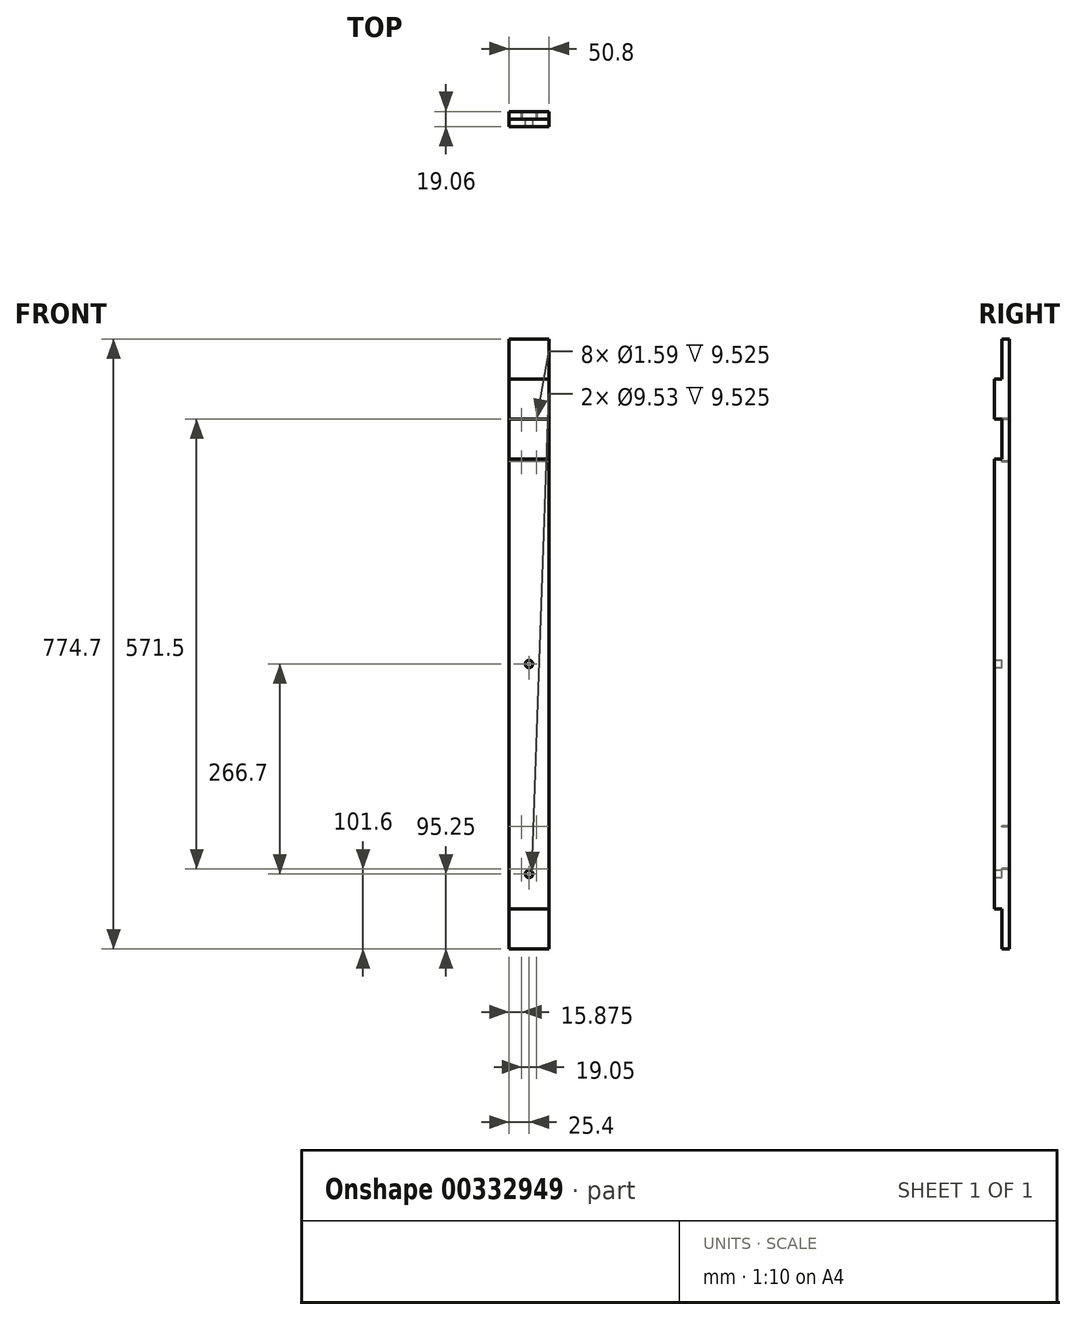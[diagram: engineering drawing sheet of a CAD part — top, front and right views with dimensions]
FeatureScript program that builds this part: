
annotation { "Feature Type Name" : "Feature", "Feature Type Description" : "" }
export const myFeature = defineFeature(function(context is Context, id is Id, definition is map)
    precondition{}
    {
        {
            var Q0;
            Q0=qCreatedBy(makeId("Top.planeOp"),FACE);
            var sketch = newSketch(context, id + "F0", { "sketchPlane" : qUnion([Q0])});
            skLineSegment(sketch, "E0.bottom", {"start": v(25.4, 9.53) * mm, "end": v(-25.4, 9.53) * mm});
            skLineSegment(sketch, "E0.top", {"start": v(25.4, -9.53) * mm, "end": v(-25.4, -9.53) * mm});
            skLineSegment(sketch, "E0.left", {"start": v(25.4, 9.53) * mm, "end": v(25.4, -9.52) * mm});
            skLineSegment(sketch, "E0.right", {"start": v(-25.4, 9.53) * mm, "end": v(-25.4, -9.53) * mm});
            skPoint(sketch, "E0.middle", {"position": v(0, 0) * mm});
            skSolve(sketch);
        }
        {
            var Q0;
            Q0=makeQuery(id+"F0.imprint","IMPRINT",FACE,{"disambiguationData":[TD([[makeQuery(id+"F0.imprint","IMPRINT",EDGE,{"derivedFrom":sQuery(id+"F0.wireOp",EDGE,"E0.bottom")}),1.0]])]});
            var Q1;
            Q1=qSketchRegion(id+"F2",true);
            extrude(context, id + "F1", {"entities" : qUnion([Q0, Q1]), "depth" : 774.7 * mm});
        }
        {
            var Q0;
            Q0=qCreatedBy(makeId("Front.planeOp"),FACE);
            var sketch = newSketch(context, id + "F2", { "sketchPlane" : qUnion([Q0])});
            skLineSegment(sketch, "E1.bottom", {"start": v(-38.77, 0) * mm, "end": v(83.66, 0) * mm});
            skLineSegment(sketch, "E1.top", {"start": v(-38.77, 50.8) * mm, "end": v(83.66, 50.8) * mm});
            skLineSegment(sketch, "E1.left", {"start": v(-38.77, 0) * mm, "end": v(-38.77, 50.8) * mm});
            skLineSegment(sketch, "E1.right", {"start": v(83.66, 0) * mm, "end": v(83.66, 50.8) * mm});
            skLineSegment(sketch, "E2.bottom", {"start": v(-210.36, 723.9) * mm, "end": v(132.8, 723.9) * mm});
            skLineSegment(sketch, "E2.top", {"start": v(-210.36, 774.7) * mm, "end": v(132.8, 774.7) * mm});
            skLineSegment(sketch, "E2.left", {"start": v(-210.36, 723.9) * mm, "end": v(-210.36, 774.7) * mm});
            skLineSegment(sketch, "E2.right", {"start": v(132.8, 723.9) * mm, "end": v(132.8, 774.7) * mm});
            skLineSegment(sketch, "E3.bottom", {"start": v(-160.47, 673.1) * mm, "end": v(92.9, 673.1) * mm});
            skLineSegment(sketch, "E3.top", {"start": v(-160.47, 622.3) * mm, "end": v(92.9, 622.3) * mm});
            skLineSegment(sketch, "E3.left", {"start": v(-160.47, 673.1) * mm, "end": v(-160.47, 622.3) * mm});
            skLineSegment(sketch, "E3.right", {"start": v(92.9, 673.1) * mm, "end": v(92.9, 622.3) * mm});
            skSolve(sketch);
        }
        {
            var Q0;
            Q0=qSketchRegion(id+"F2",true);
            extrude(context, id + "F3", {"entities" : qUnion([Q0]), "operationType" : NewBodyOperationType.REMOVE, "depth" : 25.4 * mm});
        }
        {
            var Q0;
            Q0=qCreatedBy(makeId("Front.planeOp"),FACE);
            var sketch = newSketch(context, id + "F4", { "sketchPlane" : qUnion([Q0])});
            skCircle(sketch, "E4", {"center": v(9.53, 101.6) * mm, "radius": 0.8 * mm});
            skCircle(sketch, "E5", {"center": v(9.52, 155.58) * mm, "radius": 0.8 * mm});
            skCircle(sketch, "E6", {"center": v(9.52, 619.12) * mm, "radius": 0.8 * mm});
            skCircle(sketch, "E7", {"center": v(9.52, 673.1) * mm, "radius": 0.8 * mm});
            skLineSegment(sketch, "E8", {"start": v(0, 0) * mm, "end": v(0, 1192.46) * mm, "construction": true});
            skLineSegment(sketch, "E9.bottom", {"start": v(9.52, 101.6) * mm, "end": v(-9.52, 101.6) * mm, "construction": true});
            skLineSegment(sketch, "E9.top", {"start": v(9.52, 673.1) * mm, "end": v(-9.53, 673.1) * mm, "construction": true});
            skLineSegment(sketch, "E9.left", {"start": v(9.53, 101.6) * mm, "end": v(9.52, 673.1) * mm, "construction": true});
            skLineSegment(sketch, "E9.right", {"start": v(-9.53, 101.6) * mm, "end": v(-9.53, 673.1) * mm, "construction": true});
            skCircle(sketch, "E10", {"center": v(-9.53, 619.12) * mm, "radius": 0.8 * mm});
            skCircle(sketch, "E11", {"center": v(-9.53, 673.1) * mm, "radius": 0.8 * mm});
            skCircle(sketch, "E12", {"center": v(-9.53, 101.6) * mm, "radius": 0.8 * mm});
            skCircle(sketch, "E13", {"center": v(-9.53, 155.58) * mm, "radius": 0.8 * mm});
            skSolve(sketch);
        }
        {
            var Q0;
            Q0=qSketchRegion(id+"F4",true);
            extrude(context, id + "F5", {"entities" : qUnion([Q0]), "operationType" : NewBodyOperationType.REMOVE, "oppositeDirection" : true, "depth" : 25.4 * mm});
        }
        {
            var Q0;
            Q0=qCreatedBy(makeId("Front.planeOp"),FACE);
            var sketch = newSketch(context, id + "F6", { "sketchPlane" : qUnion([Q0])});
            skCircle(sketch, "E14", {"center": v(0, 95.25) * mm, "radius": 4.76 * mm});
            skCircle(sketch, "E15", {"center": v(0, 361.95) * mm, "radius": 4.76 * mm});
            skSolve(sketch);
        }
        {
            var Q0;
            Q0=qSketchRegion(id+"F6",true);
            extrude(context, id + "F7", {"entities" : qUnion([Q0]), "operationType" : NewBodyOperationType.REMOVE, "depth" : 25.4 * mm});
        }
    });
